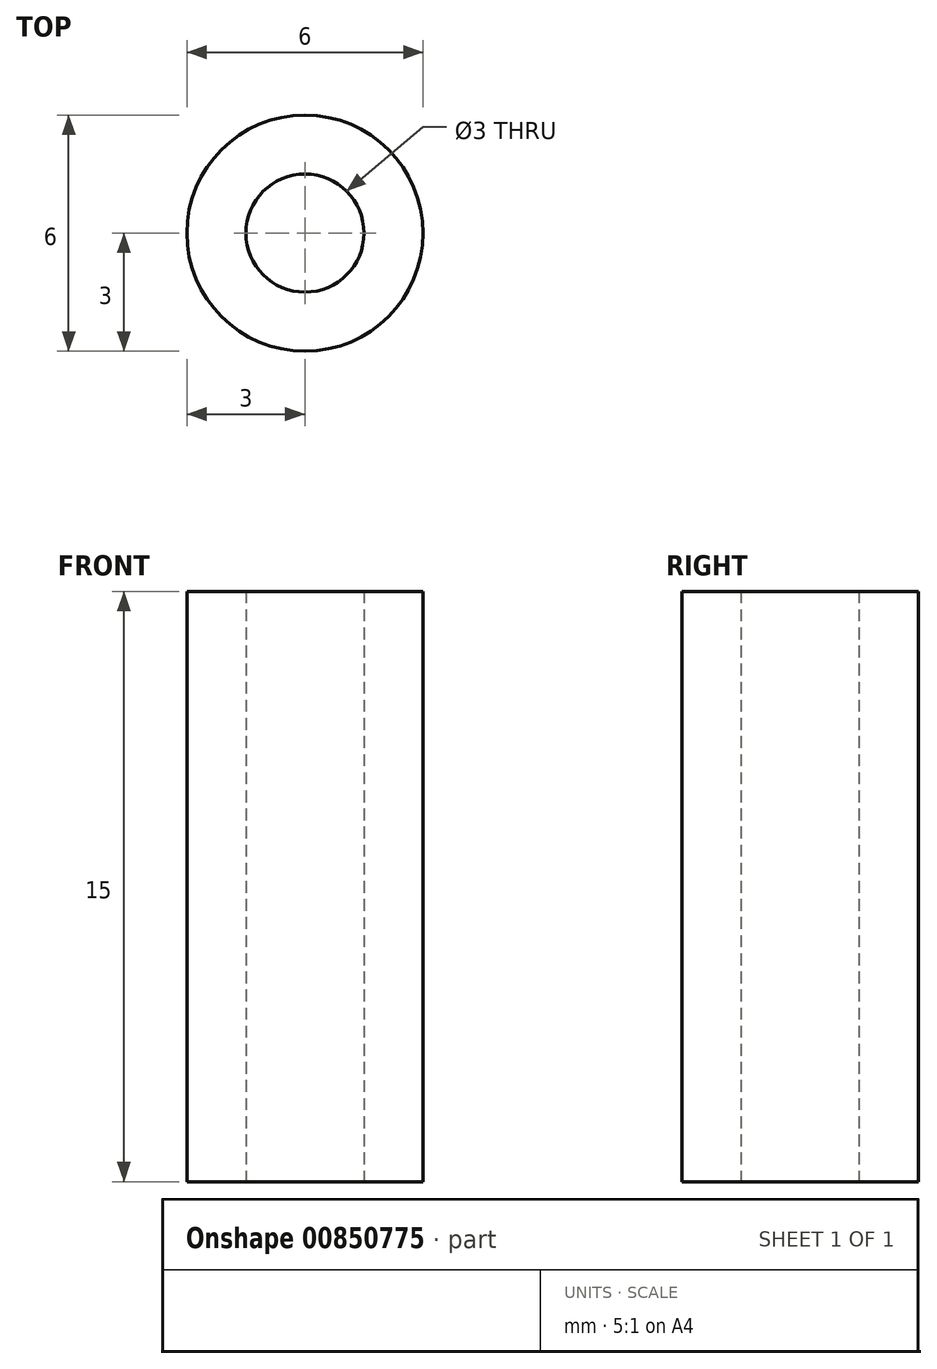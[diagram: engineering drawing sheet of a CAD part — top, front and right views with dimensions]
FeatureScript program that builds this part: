
annotation { "Feature Type Name" : "Feature", "Feature Type Description" : "" }
export const myFeature = defineFeature(function(context is Context, id is Id, definition is map)
    precondition{}
    {
        {
            var Q0;
            Q0=qCreatedBy(makeId("Top.planeOp"),FACE);
            var sketch = newSketch(context, id + "F0", { "sketchPlane" : qUnion([Q0])});
            skCircle(sketch, "E0", {"center": v(0, 0) * mm, "radius": 1.5 * mm});
            skCircle(sketch, "E1", {"center": v(0, 0) * mm, "radius": 3 * mm});
            skSolve(sketch);
        }
        {
            var Q0;
            Q0 = qSketchRegion(id + "F0", true);
            extrude(context, id + "F1", {"entities" : qUnion([Q0]), "depth" : 15 * mm, "offsetDistance" : 25 * mm});
        }
    });
